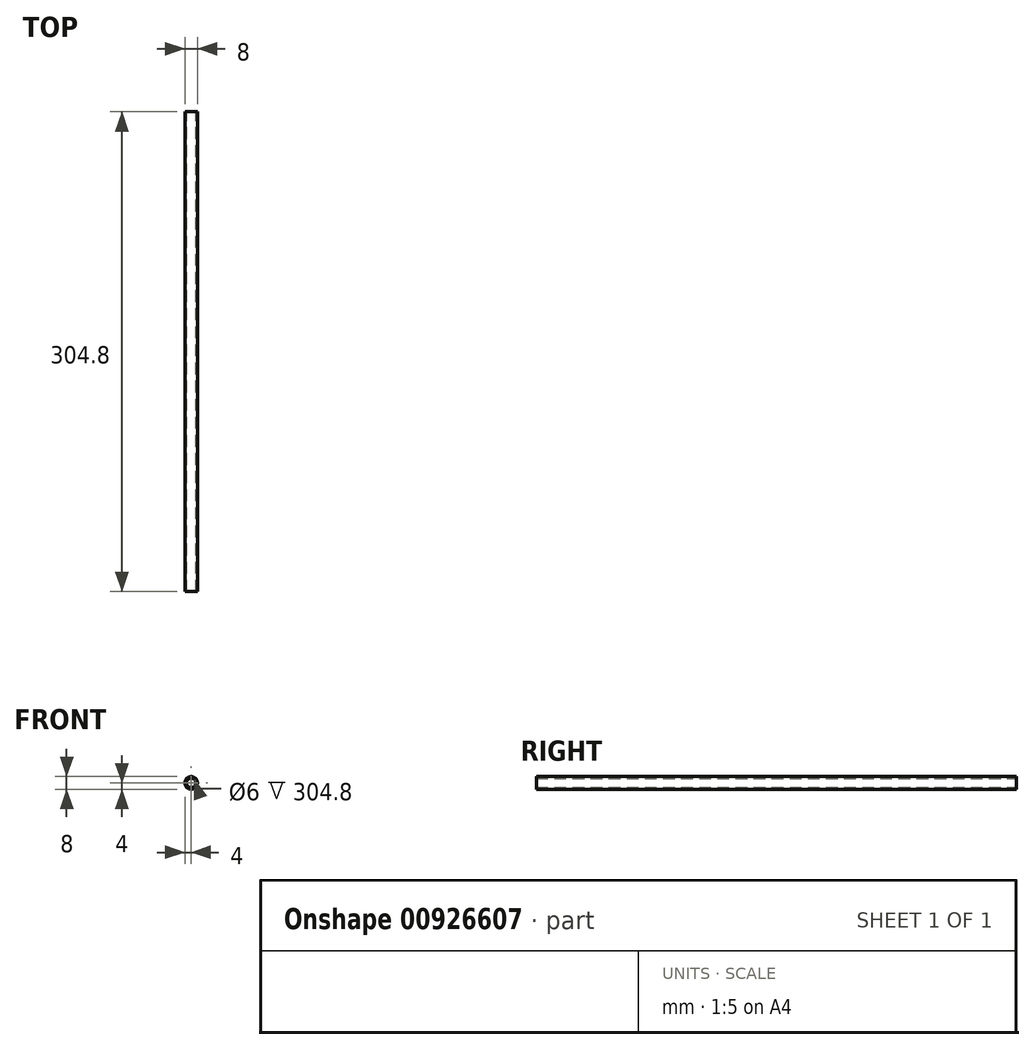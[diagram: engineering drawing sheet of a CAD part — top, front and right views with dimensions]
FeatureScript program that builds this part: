
annotation { "Feature Type Name" : "Feature", "Feature Type Description" : "" }
export const myFeature = defineFeature(function(context is Context, id is Id, definition is map)
    precondition{}
    {
        {
            var Q0;
            Q0=qCreatedBy(makeId("Front.planeOp"),FACE);
            var sketch = newSketch(context, id + "F0", { "sketchPlane" : qUnion([Q0])});
            skCircle(sketch, "E0", {"center": v(0, 0) * mm, "radius": 4 * mm});
            skCircle(sketch, "E1", {"center": v(0, 0) * mm, "radius": 3 * mm});
            skSolve(sketch);
        }
        {
            var Q0;
            Q0=makeQuery(id+"F0.imprint","IMPRINT",FACE,{"disambiguationData":[TD([[makeQuery(id+"F0.imprint","IMPRINT",EDGE,{"derivedFrom":sQuery(id+"F0.wireOp",EDGE,"E0")}),1.0]])]});
            extrude(context, id + "F1", {"entities" : qUnion([Q0]), "depth" : 304.8 * mm, "offsetDistance" : 25.4 * mm});
        }
    });
